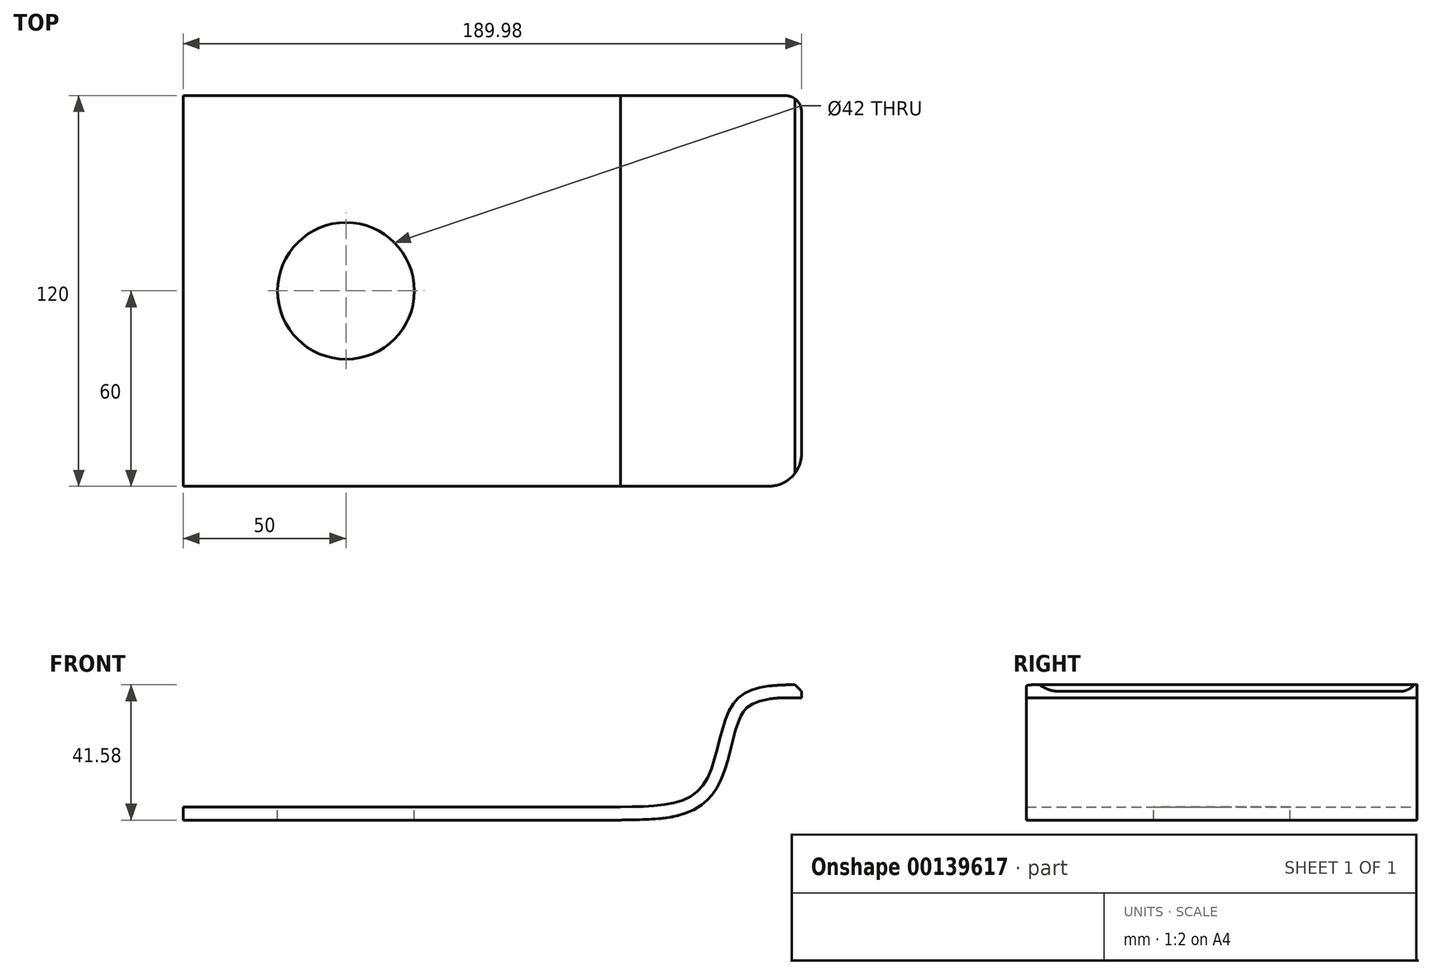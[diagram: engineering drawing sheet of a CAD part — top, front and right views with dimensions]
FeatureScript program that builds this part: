
annotation { "Feature Type Name" : "Feature", "Feature Type Description" : "" }
export const myFeature = defineFeature(function(context is Context, id is Id, definition is map)
    precondition{}
    {
        {
            var Q0;
            Q0=qCreatedBy(makeId("Front.planeOp"),FACE);
            var sketch = newSketch(context, id + "F0", { "sketchPlane" : qUnion([Q0])});
            skLineSegment(sketch, "E0.bottom", {"start": v(0, 0) * mm, "end": v(134.42, 0) * mm});
            skLineSegment(sketch, "E0.top", {"start": v(0, 4) * mm, "end": v(134.42, 4) * mm});
            skLineSegment(sketch, "E0.left", {"start": v(0, 0) * mm, "end": v(0, 4) * mm});
            skFitSpline(sketch, "E1", {"points": [v(134.42, 4) * mm, v(159.3, 10.16) * mm, v(168.58, 35.13) * mm, v(190, 41.58) * mm], "startDerivative": vector(93.18, 2.3) * mm, "endDerivative": vector(101.36, -0.8) * mm});
            skFitSpline(sketch, "E2.0", {"points": [v(134.52, 0) * mm, v(136.44, 0.05) * mm, v(140.28, 0.12) * mm, v(145.87, 0.4) * mm, v(150.35, 1.03) * mm, v(153.79, 1.94) * mm, v(156.28, 2.9) * mm, v(158.25, 3.97) * mm, v(159.74, 5.02) * mm, v(160.8, 5.91) * mm, v(161.8, 6.9) * mm, v(162.71, 8) * mm, v(163.52, 9.15) * mm, v(164.48, 10.75) * mm, v(165.47, 12.83) * mm, v(166.43, 15.4) * mm, v(167.23, 18.03) * mm, v(167.93, 20.65) * mm, v(168.57, 23.23) * mm, v(169.2, 25.7) * mm, v(169.85, 28) * mm, v(170.42, 29.72) * mm, v(170.9, 30.94) * mm, v(171.28, 31.77) * mm, v(171.6, 32.38) * mm, v(171.85, 32.81) * mm, v(172.1, 33.21) * mm, v(172.44, 33.67) * mm, v(173, 34.31) * mm, v(173.75, 34.99) * mm, v(174.83, 35.67) * mm, v(176.13, 36.26) * mm, v(177.72, 36.74) * mm, v(180.23, 37.23) * mm, v(184.09, 37.57) * mm, v(187.9, 37.6) * mm, v(189.97, 37.58) * mm]});
            skLineSegment(sketch, "E3", {"start": v(190, 41.58) * mm, "end": v(189.97, 37.58) * mm});
            skLineSegment(sketch, "E4", {"start": v(134.42, 0) * mm, "end": v(134.52, 0) * mm});
            skSolve(sketch);
        }
        {
            var Q0;
            Q0=makeQuery(id+"F0.imprint","IMPRINT",FACE,{"disambiguationData":[TD([[makeQuery(id+"F0.imprint","IMPRINT",EDGE,{"derivedFrom":sQuery(id+"F0.wireOp",EDGE,"E0.bottom")}),1.0]])]});
            extrude(context, id + "F1", {"entities" : qUnion([Q0]), "depth" : 120 * mm, "symmetric" : true});
        }
        {
            var Q0;
            Q0=makeQuery(id+"F1.opExtrude","SWEPT_FACE",FACE,{"disambiguationData":[OSD([sQuery(id+"F0.wireOp",EDGE,"E0.top")])]});
            var sketch = newSketch(context, id + "F2", { "sketchPlane" : qUnion([Q0])});
            skLineSegment(sketch, "E5", {"start": v(0, 0) * mm, "end": v(85.1, 0) * mm, "construction": true});
            skCircle(sketch, "E6", {"center": v(50, 0) * mm, "radius": 21 * mm});
            skSolve(sketch);
        }
        {
            var Q0;
            Q0 = qSketchRegion(id + "F2", true);
            extrude(context, id + "F3", {"entities" : qUnion([Q0]), "operationType" : NewBodyOperationType.REMOVE, "oppositeDirection" : true, "depth" : 25.4 * mm});
        }
        {
            var Q0;
            Q0=makeQuery(id+"F1.opExtrude","SWEPT_EDGE",EDGE,{"disambiguationData":[OSD([sQuery(id+"F0.wireOp",EDGE,"E1"),sQuery(id+"F0.wireOp",EDGE,"E3")])]});
            chamfer(context, id + "F4", {"entities" : qUnion([Q0]), "width" : 2 * mm, "tangentPropagation" : true});
        }
        {
            var Q0;
            Q0=makeQuery(id+"F1.opExtrude","CAP_EDGE",EDGE,{"disambiguationData":[OSD([sQuery(id+"F0.wireOp",EDGE,"E3")])],"isStart":false});
            fillet(context, id + "F5", {"entities" : qUnion([Q0]), "radius" : 10 * mm, "tangentPropagation" : true, "allowEdgeOverflow" : false});
        }
        {
            var Q0;
            Q0=makeQuery(id+"F1.opExtrude","CAP_EDGE",EDGE,{"disambiguationData":[OSD([sQuery(id+"F0.wireOp",EDGE,"E3")])],"isStart":true});
            fillet(context, id + "F6", {"entities" : qUnion([Q0]), "radius" : 5 * mm, "tangentPropagation" : true, "allowEdgeOverflow" : false});
        }
    });
